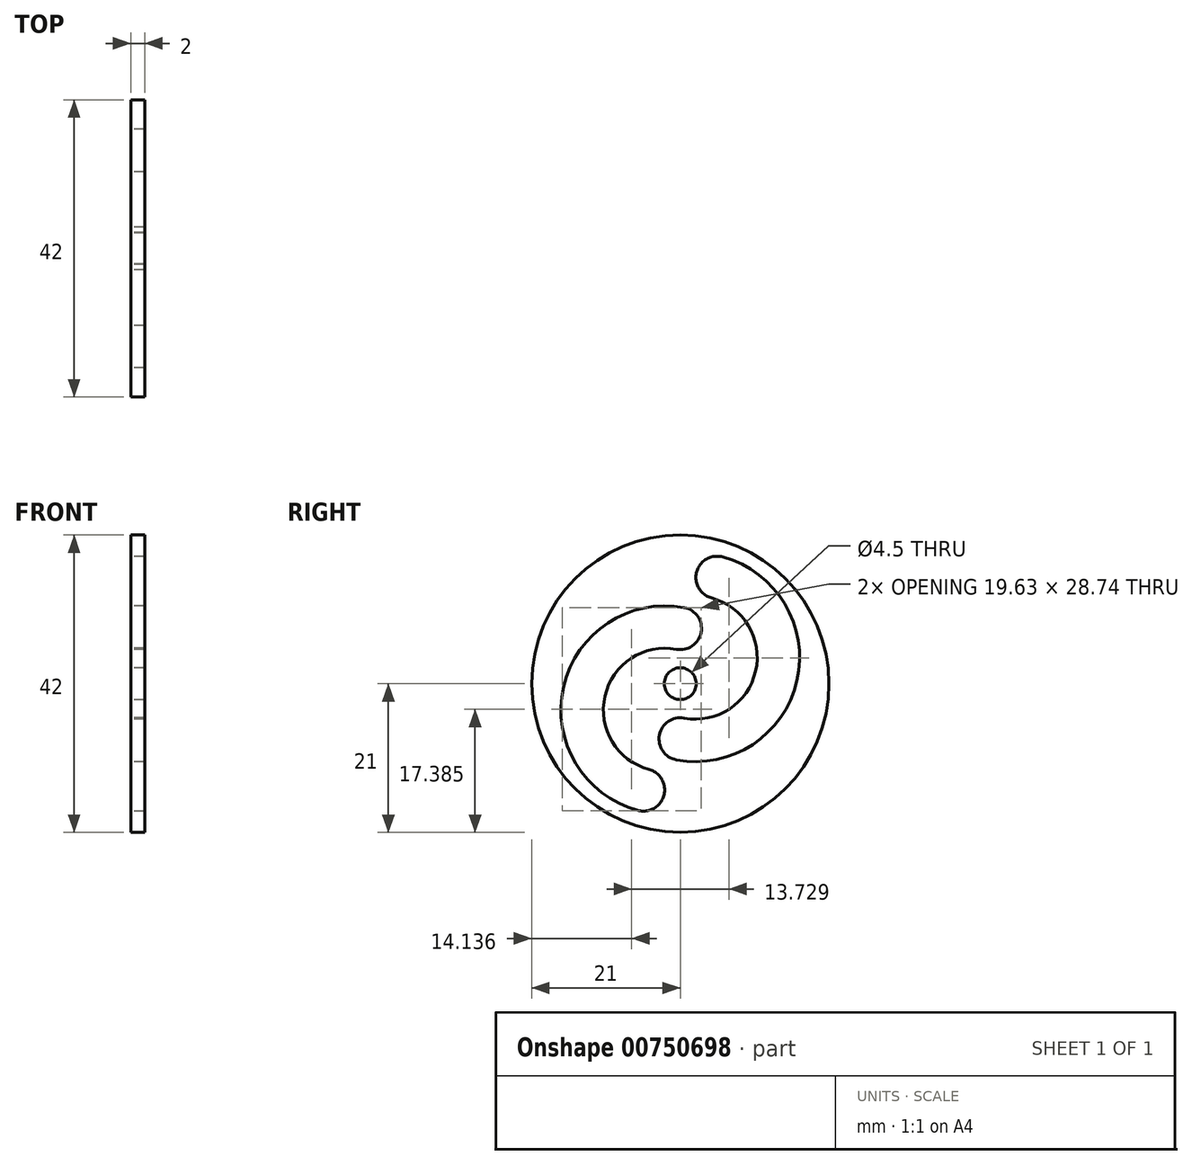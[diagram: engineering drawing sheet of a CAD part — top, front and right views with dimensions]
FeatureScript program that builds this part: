
annotation { "Feature Type Name" : "Feature", "Feature Type Description" : "" }
export const myFeature = defineFeature(function(context is Context, id is Id, definition is map)
    precondition{}
    {
        {
            var Q0;
            Q0=qCreatedBy(makeId("Right.planeOp"),FACE);
            var sketch = newSketch(context, id + "F0", { "sketchPlane" : qUnion([Q0])});
            skArc(sketch, "E0", {"start": v(0.55, -4.86) * mm, "mid": v(-2.95, -7.26) * mm, "end": v(-0.55, -10.76) * mm});
            skCircle(sketch, "E1", {"center": v(0, 0) * mm, "radius": 21 * mm});
            skArc(sketch, "E2", {"start": v(-0.55, -10.76) * mm, "mid": v(16.5, 0.43) * mm, "end": v(5.99, 17.9) * mm});
            skArc(sketch, "E3", {"start": v(5.99, 17.9) * mm, "mid": v(2.31, 15.8) * mm, "end": v(4.42, 12.12) * mm});
            skArc(sketch, "E4", {"start": v(4.42, 12.12) * mm, "mid": v(10.64, 1.77) * mm, "end": v(0.55, -4.86) * mm});
            skArc(sketch, "E5.1.0", {"start": v(-5.99, -17.9) * mm, "mid": v(-2.31, -15.8) * mm, "end": v(-4.42, -12.12) * mm});
            skArc(sketch, "E5.1.1", {"start": v(0.55, 10.76) * mm, "mid": v(-16.5, -0.43) * mm, "end": v(-5.99, -17.9) * mm});
            skArc(sketch, "E5.1.2", {"start": v(-4.42, -12.12) * mm, "mid": v(-10.64, -1.77) * mm, "end": v(-0.55, 4.86) * mm});
            skArc(sketch, "E5.1.3", {"start": v(-0.55, 4.86) * mm, "mid": v(2.95, 7.26) * mm, "end": v(0.55, 10.76) * mm});
            skCircle(sketch, "E6", {"center": v(0, 0) * mm, "radius": 2.25 * mm});
            skSolve(sketch);
        }
        {
            var Q0;
            Q0 = qSketchRegion(id + "F0", true);
            extrude(context, id + "F1", {"entities" : qUnion([Q0]), "depth" : 2 * mm, "offsetDistance" : 25 * mm});
        }
    });
